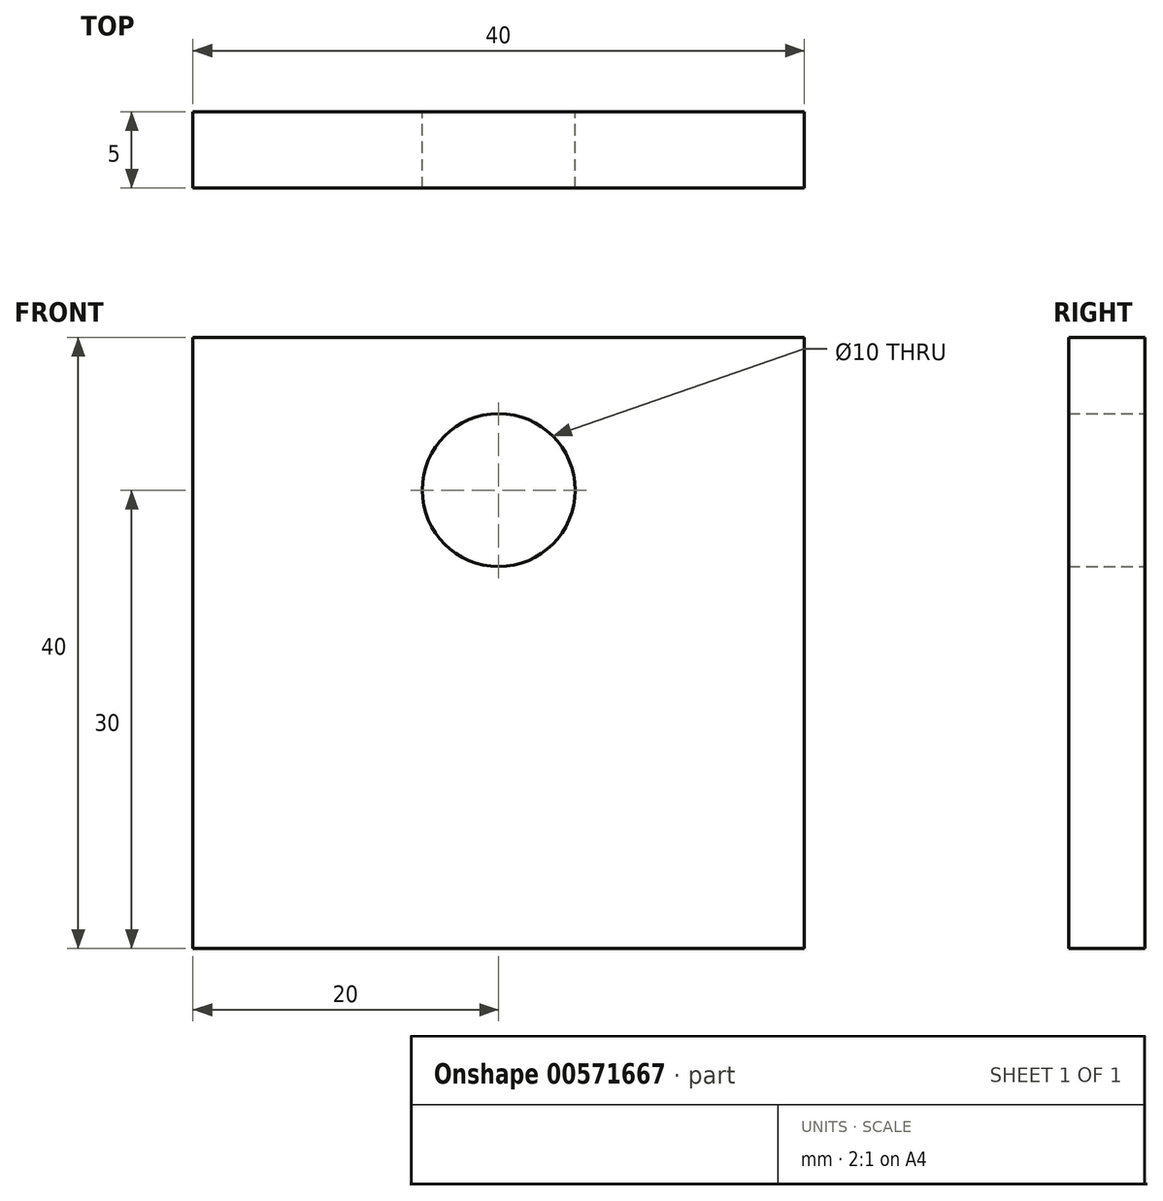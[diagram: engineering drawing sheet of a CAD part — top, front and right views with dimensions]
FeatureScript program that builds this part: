
annotation { "Feature Type Name" : "Feature", "Feature Type Description" : "" }
export const myFeature = defineFeature(function(context is Context, id is Id, definition is map)
    precondition{}
    {
        {
            var Q0;
            Q0=qCreatedBy(makeId("Top.planeOp"),FACE);
            var sketch = newSketch(context, id + "F0", { "sketchPlane" : qUnion([Q0])});
            skLineSegment(sketch, "E0.bottom", {"start": v(20, 2.5) * mm, "end": v(-20, 2.5) * mm});
            skLineSegment(sketch, "E0.top", {"start": v(20, -2.5) * mm, "end": v(-20, -2.5) * mm});
            skLineSegment(sketch, "E0.left", {"start": v(20, 2.5) * mm, "end": v(20, -2.5) * mm});
            skLineSegment(sketch, "E0.right", {"start": v(-20, 2.5) * mm, "end": v(-20, -2.5) * mm});
            skPoint(sketch, "E0.middle", {"position": v(0, 0) * mm});
            skSolve(sketch);
        }
        {
            var Q0;
            Q0 = qSketchRegion(id + "F0", true);
            extrude(context, id + "F1", {"entities" : qUnion([Q0]), "depth" : 20 * mm + 20 * mm, "offsetDistance" : 25.4 * mm});
        }
        {
            var Q0;
            Q0=makeQuery(id+"F1.opExtrude","SWEPT_FACE",FACE,{"disambiguationData":[OSD([sQuery(id+"F0.wireOp",EDGE,"E0.bottom")])]});
            var sketch = newSketch(context, id + "F2", { "sketchPlane" : qUnion([Q0])});
            skCircle(sketch, "E1", {"center": v(0, 30) * mm, "radius": 5 * mm});
            skSolve(sketch);
        }
        {
            var Q0;
            Q0=makeQuery(id+"F2.imprint","IMPRINT",FACE,{"disambiguationData":[TD([[makeQuery(id+"F2.imprint","IMPRINT",EDGE,{"derivedFrom":sQuery(id+"F2.wireOp",EDGE,"E1")}),1.0]])]});
            extrude(context, id + "F3", {"entities" : qUnion([Q0]), "operationType" : NewBodyOperationType.REMOVE, "oppositeDirection" : true, "depth" : 5 * mm, "offsetDistance" : 25.4 * mm});
        }
    });
